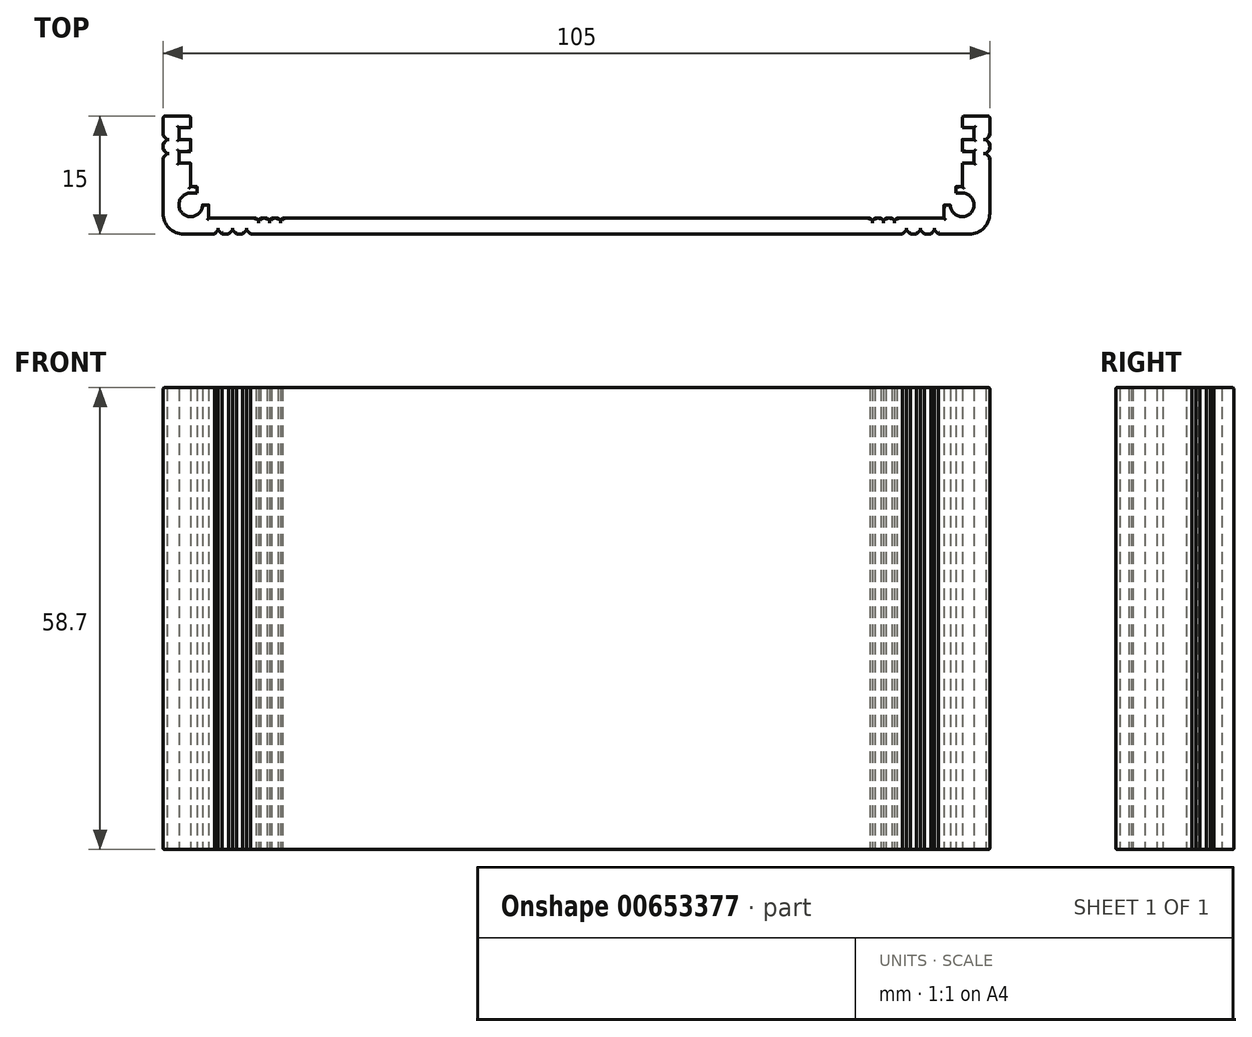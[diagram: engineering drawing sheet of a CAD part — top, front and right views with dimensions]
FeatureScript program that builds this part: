
annotation { "Feature Type Name" : "Feature", "Feature Type Description" : "" }
export const myFeature = defineFeature(function(context is Context, id is Id, definition is map)
    precondition{}
    {
        {
            var Q0;
            Q0=qCreatedBy(makeId("Top.planeOp"),FACE);
            var sketch = newSketch(context, id + "F0", { "sketchPlane" : qUnion([Q0])});
            skLineSegment(sketch, "E0.bottom", {"start": v(52.5, 15) * mm, "end": v(-52.5, 15) * mm, "construction": true});
            skLineSegment(sketch, "E0.top", {"start": v(52.5, -15) * mm, "end": v(-52.5, -15) * mm, "construction": true});
            skLineSegment(sketch, "E0.left", {"start": v(52.5, 15) * mm, "end": v(52.5, -15) * mm, "construction": true});
            skLineSegment(sketch, "E0.right", {"start": v(-52.5, 15) * mm, "end": v(-52.5, -15) * mm, "construction": true});
            skPoint(sketch, "E0.middle", {"position": v(0, 0) * mm});
            skLineSegment(sketch, "E1", {"start": v(-52.5, -15) * mm, "end": v(-46, -15) * mm});
            skLineSegment(sketch, "E2", {"start": v(-46, -15) * mm, "end": v(-45.5, -14.5) * mm});
            skLineSegment(sketch, "E3", {"start": v(-45.5, -14.5) * mm, "end": v(-45, -15) * mm});
            skLineSegment(sketch, "E4", {"start": v(-45, -15) * mm, "end": v(-44.2, -15) * mm});
            skLineSegment(sketch, "E5", {"start": v(-44.2, -15) * mm, "end": v(-43.7, -14.5) * mm});
            skLineSegment(sketch, "E6", {"start": v(-43.7, -14.5) * mm, "end": v(-43.2, -15) * mm});
            skLineSegment(sketch, "E7", {"start": v(-43.2, -15) * mm, "end": v(-42.4, -15) * mm});
            skLineSegment(sketch, "E8", {"start": v(-42.4, -15) * mm, "end": v(-41.9, -14.5) * mm});
            skLineSegment(sketch, "E9", {"start": v(-41.9, -14.5) * mm, "end": v(-41.4, -15) * mm});
            skLineSegment(sketch, "E10", {"start": v(-41.4, -15) * mm, "end": v(0, -15) * mm});
            skLineSegment(sketch, "E11.MirrorCS", {"start": v(52.5, -15) * mm, "end": v(46, -15) * mm});
            skLineSegment(sketch, "E12.MirrorCS", {"start": v(46, -15) * mm, "end": v(45.5, -14.5) * mm});
            skLineSegment(sketch, "E13.MirrorCS", {"start": v(45.5, -14.5) * mm, "end": v(45, -15) * mm});
            skLineSegment(sketch, "E14.MirrorCS", {"start": v(45, -15) * mm, "end": v(44.2, -15) * mm});
            skLineSegment(sketch, "E15.MirrorCS", {"start": v(44.2, -15) * mm, "end": v(43.7, -14.5) * mm});
            skLineSegment(sketch, "E16.MirrorCS", {"start": v(43.7, -14.5) * mm, "end": v(43.2, -15) * mm});
            skLineSegment(sketch, "E17.MirrorCS", {"start": v(43.2, -15) * mm, "end": v(42.4, -15) * mm});
            skLineSegment(sketch, "E18.MirrorCS", {"start": v(42.4, -15) * mm, "end": v(41.9, -14.5) * mm});
            skLineSegment(sketch, "E19.MirrorCS", {"start": v(41.9, -14.5) * mm, "end": v(41.4, -15) * mm});
            skLineSegment(sketch, "E20.MirrorCS", {"start": v(41.4, -15) * mm, "end": v(0, -15) * mm});
            skLineSegment(sketch, "E21", {"start": v(-52.5, 0) * mm, "end": v(-52.5, -2.5) * mm});
            skLineSegment(sketch, "E22", {"start": v(-52.5, -2.5) * mm, "end": v(-52, -3) * mm});
            skLineSegment(sketch, "E23", {"start": v(-52, -3) * mm, "end": v(-52.5, -3.5) * mm});
            skLineSegment(sketch, "E24", {"start": v(-52.5, -3.5) * mm, "end": v(-52.5, -4.3) * mm});
            skLineSegment(sketch, "E25", {"start": v(-52.5, -4.3) * mm, "end": v(-52, -4.8) * mm});
            skLineSegment(sketch, "E26", {"start": v(-52, -4.8) * mm, "end": v(-52.5, -5.3) * mm});
            skLineSegment(sketch, "E27", {"start": v(-52.5, -5.3) * mm, "end": v(-52.5, -15) * mm});
            skLineSegment(sketch, "E28.MirrorCS", {"start": v(52.5, 0) * mm, "end": v(52.5, -2.5) * mm});
            skLineSegment(sketch, "E29.MirrorCS", {"start": v(52.5, -2.5) * mm, "end": v(52, -3) * mm});
            skLineSegment(sketch, "E30.MirrorCS", {"start": v(52, -3) * mm, "end": v(52.5, -3.5) * mm});
            skLineSegment(sketch, "E31.MirrorCS", {"start": v(52.5, -4.3) * mm, "end": v(52, -4.8) * mm});
            skLineSegment(sketch, "E32.MirrorCS", {"start": v(52.5, -3.5) * mm, "end": v(52.5, -4.3) * mm});
            skLineSegment(sketch, "E33.MirrorCS", {"start": v(52, -4.8) * mm, "end": v(52.5, -5.3) * mm});
            skLineSegment(sketch, "E34.MirrorCS", {"start": v(52.5, -5.3) * mm, "end": v(52.5, -15) * mm});
            skLineSegment(sketch, "E35", {"start": v(-52.5, 0) * mm, "end": v(-49, 0) * mm});
            skLineSegment(sketch, "E36", {"start": v(-49, 0) * mm, "end": v(-49, -1.5) * mm});
            skLineSegment(sketch, "E37", {"start": v(-49, -1.5) * mm, "end": v(-50.5, -1.5) * mm});
            skLineSegment(sketch, "E38", {"start": v(-50.5, -1.5) * mm, "end": v(-50.5, -3) * mm});
            skLineSegment(sketch, "E39", {"start": v(-50.5, -3) * mm, "end": v(-49, -3) * mm});
            skLineSegment(sketch, "E40", {"start": v(-49, -3) * mm, "end": v(-49, -4.5) * mm});
            skLineSegment(sketch, "E41", {"start": v(-49, -4.5) * mm, "end": v(-50.5, -4.5) * mm});
            skLineSegment(sketch, "E42", {"start": v(-50.5, -4.5) * mm, "end": v(-50.5, -6) * mm});
            skLineSegment(sketch, "E43", {"start": v(-50.5, -6) * mm, "end": v(-49, -6) * mm});
            skLineSegment(sketch, "E44", {"start": v(-49, -6) * mm, "end": v(-49, -9) * mm});
            skCircle(sketch, "E45", {"center": v(-49, -11.3) * mm, "radius": 1.5 * mm, "construction": true});
            skPoint(sketch, "E45.second.point", {"position": v(-49, -12.8) * mm});
            skPoint(sketch, "E45.third.point", {"position": v(-47.5, -11.3) * mm});
            skLineSegment(sketch, "E46", {"start": v(-49, -12.8) * mm, "end": v(-49, -9.8) * mm, "construction": true});
            skArc(sketch, "E47", {"start": v(-49, -9.8) * mm, "mid": v(-50.06, -12.36) * mm, "end": v(-47.5, -11.3) * mm});
            skLineSegment(sketch, "E48", {"start": v(-47.5, -11.3) * mm, "end": v(-47.5, -11.3) * mm});
            skLineSegment(sketch, "E49", {"start": v(-46.7, -13) * mm, "end": v(-40.7, -13) * mm});
            skLineSegment(sketch, "E50", {"start": v(-40.7, -13) * mm, "end": v(-40.4, -13.3) * mm});
            skLineSegment(sketch, "E51", {"start": v(-40.4, -13.3) * mm, "end": v(-40.1, -13) * mm});
            skLineSegment(sketch, "E52", {"start": v(-40.1, -13) * mm, "end": v(-39.3, -13) * mm});
            skLineSegment(sketch, "E53", {"start": v(-39.3, -13) * mm, "end": v(-39, -13.3) * mm});
            skLineSegment(sketch, "E54", {"start": v(-39, -13.3) * mm, "end": v(-38.7, -13) * mm});
            skLineSegment(sketch, "E55", {"start": v(-38.7, -13) * mm, "end": v(-37.9, -13) * mm});
            skLineSegment(sketch, "E56", {"start": v(-37.9, -13) * mm, "end": v(-37.6, -13.3) * mm});
            skLineSegment(sketch, "E57", {"start": v(-37.6, -13.3) * mm, "end": v(-37.3, -13) * mm});
            skLineSegment(sketch, "E58", {"start": v(-37.3, -13) * mm, "end": v(0, -13) * mm});
            skLineSegment(sketch, "E59", {"start": v(-47.5, -11.3) * mm, "end": v(-46.7, -11.3) * mm});
            skLineSegment(sketch, "E60", {"start": v(-46.7, -11.3) * mm, "end": v(-46.7, -13) * mm});
            skLineSegment(sketch, "E61.MirrorCS", {"start": v(37.3, -13) * mm, "end": v(0, -13) * mm});
            skLineSegment(sketch, "E62.MirrorCS", {"start": v(37.6, -13.3) * mm, "end": v(37.3, -13) * mm});
            skLineSegment(sketch, "E63.MirrorCS", {"start": v(37.9, -13) * mm, "end": v(37.6, -13.3) * mm});
            skLineSegment(sketch, "E64.MirrorCS", {"start": v(39, -13.3) * mm, "end": v(38.7, -13) * mm});
            skLineSegment(sketch, "E65.MirrorCS", {"start": v(39.3, -13) * mm, "end": v(39, -13.3) * mm});
            skLineSegment(sketch, "E66.MirrorCS", {"start": v(40.4, -13.3) * mm, "end": v(40.1, -13) * mm});
            skLineSegment(sketch, "E67.MirrorCS", {"start": v(40.7, -13) * mm, "end": v(40.4, -13.3) * mm});
            skLineSegment(sketch, "E68.MirrorCS", {"start": v(46.7, -13) * mm, "end": v(40.7, -13) * mm});
            skLineSegment(sketch, "E69.MirrorCS", {"start": v(46.7, -11.3) * mm, "end": v(46.7, -13) * mm});
            skLineSegment(sketch, "E70.MirrorCS", {"start": v(49, -6) * mm, "end": v(49, -9) * mm});
            skLineSegment(sketch, "E71.MirrorCS", {"start": v(50.5, -6) * mm, "end": v(49, -6) * mm});
            skLineSegment(sketch, "E72.MirrorCS", {"start": v(50.5, -4.5) * mm, "end": v(50.5, -6) * mm});
            skLineSegment(sketch, "E73.MirrorCS", {"start": v(49, -4.5) * mm, "end": v(50.5, -4.5) * mm});
            skLineSegment(sketch, "E74.MirrorCS", {"start": v(49, -3) * mm, "end": v(49, -4.5) * mm});
            skLineSegment(sketch, "E75.MirrorCS", {"start": v(50.5, -3) * mm, "end": v(49, -3) * mm});
            skLineSegment(sketch, "E76.MirrorCS", {"start": v(50.5, -1.5) * mm, "end": v(50.5, -3) * mm});
            skLineSegment(sketch, "E77.MirrorCS", {"start": v(49, -1.5) * mm, "end": v(50.5, -1.5) * mm});
            skLineSegment(sketch, "E78.MirrorCS", {"start": v(49, 0) * mm, "end": v(49, -1.5) * mm});
            skLineSegment(sketch, "E79.MirrorCS", {"start": v(52.5, 0) * mm, "end": v(49, 0) * mm});
            skLineSegment(sketch, "E80.MirrorCS", {"start": v(38.7, -13) * mm, "end": v(37.9, -13) * mm});
            skLineSegment(sketch, "E81.MirrorCS", {"start": v(40.1, -13) * mm, "end": v(39.3, -13) * mm});
            skLineSegment(sketch, "E82", {"start": v(-49, -9) * mm, "end": v(-48.2, -9) * mm});
            skLineSegment(sketch, "E83", {"start": v(-48.2, -9) * mm, "end": v(-48.2, -9.8) * mm});
            skLineSegment(sketch, "E84", {"start": v(-48.2, -9.8) * mm, "end": v(-49, -9.8) * mm});
            skLineSegment(sketch, "E85", {"start": v(-50.5, -11.3) * mm, "end": v(-47.5, -11.3) * mm, "construction": true});
            skLineSegment(sketch, "E86", {"start": v(-50.5, -11.3) * mm, "end": v(-50.5, -1.5) * mm, "construction": true});
            skArc(sketch, "E87.MirrorCS", {"start": v(49, -9.8) * mm, "mid": v(50.06, -12.36) * mm, "end": v(47.5, -11.3) * mm});
            skLineSegment(sketch, "E88.MirrorCS", {"start": v(49, -9) * mm, "end": v(48.2, -9) * mm});
            skLineSegment(sketch, "E89.MirrorCS", {"start": v(48.2, -9.8) * mm, "end": v(49, -9.8) * mm});
            skLineSegment(sketch, "E90.MirrorCS", {"start": v(48.2, -9) * mm, "end": v(48.2, -9.8) * mm});
            skLineSegment(sketch, "E91.MirrorCS", {"start": v(47.5, -11.3) * mm, "end": v(46.7, -11.3) * mm});
            skSolve(sketch);
        }
        {
            var Q0;
            Q0=makeQuery(id+"F0.imprint","IMPRINT",FACE,{"disambiguationData":[TD([[makeQuery(id+"F0.imprint","IMPRINT",EDGE,{"derivedFrom":sQuery(id+"F0.wireOp",EDGE,"E1")}),1.0]])]});
            extrude(context, id + "F1", {"entities" : qUnion([Q0]), "depth" : 58.7 * mm, "offsetDistance" : 25.4 * mm});
        }
        {
            var Q0;
            Q0=makeQuery(id+"F1.opExtrude","CAP_FACE",FACE,{"disambiguationData":[OSD([sQuery(id+"F0.wireOp",EDGE,"E1"),sQuery(id+"F0.wireOp",EDGE,"E2"),sQuery(id+"F0.wireOp",EDGE,"E3"),sQuery(id+"F0.wireOp",EDGE,"E4"),sQuery(id+"F0.wireOp",EDGE,"E5"),sQuery(id+"F0.wireOp",EDGE,"E6"),sQuery(id+"F0.wireOp",EDGE,"E7"),sQuery(id+"F0.wireOp",EDGE,"E8"),sQuery(id+"F0.wireOp",EDGE,"E9"),sQuery(id+"F0.wireOp",EDGE,"E10"),sQuery(id+"F0.wireOp",EDGE,"E11.MirrorCS"),sQuery(id+"F0.wireOp",EDGE,"E12.MirrorCS"),sQuery(id+"F0.wireOp",EDGE,"E13.MirrorCS"),sQuery(id+"F0.wireOp",EDGE,"E14.MirrorCS"),sQuery(id+"F0.wireOp",EDGE,"E15.MirrorCS"),sQuery(id+"F0.wireOp",EDGE,"E16.MirrorCS"),sQuery(id+"F0.wireOp",EDGE,"E17.MirrorCS"),sQuery(id+"F0.wireOp",EDGE,"E18.MirrorCS"),sQuery(id+"F0.wireOp",EDGE,"E19.MirrorCS"),sQuery(id+"F0.wireOp",EDGE,"E20.MirrorCS"),sQuery(id+"F0.wireOp",EDGE,"E21"),sQuery(id+"F0.wireOp",EDGE,"E22"),sQuery(id+"F0.wireOp",EDGE,"E23"),sQuery(id+"F0.wireOp",EDGE,"E24"),sQuery(id+"F0.wireOp",EDGE,"E25"),sQuery(id+"F0.wireOp",EDGE,"E26"),sQuery(id+"F0.wireOp",EDGE,"E27"),sQuery(id+"F0.wireOp",EDGE,"E28.MirrorCS"),sQuery(id+"F0.wireOp",EDGE,"E29.MirrorCS"),sQuery(id+"F0.wireOp",EDGE,"E30.MirrorCS"),sQuery(id+"F0.wireOp",EDGE,"E31.MirrorCS"),sQuery(id+"F0.wireOp",EDGE,"E32.MirrorCS"),sQuery(id+"F0.wireOp",EDGE,"E33.MirrorCS"),sQuery(id+"F0.wireOp",EDGE,"E34.MirrorCS"),sQuery(id+"F0.wireOp",EDGE,"E35"),sQuery(id+"F0.wireOp",EDGE,"E36"),sQuery(id+"F0.wireOp",EDGE,"E37"),sQuery(id+"F0.wireOp",EDGE,"E38"),sQuery(id+"F0.wireOp",EDGE,"E39"),sQuery(id+"F0.wireOp",EDGE,"E40"),sQuery(id+"F0.wireOp",EDGE,"E41"),sQuery(id+"F0.wireOp",EDGE,"E42"),sQuery(id+"F0.wireOp",EDGE,"E43"),sQuery(id+"F0.wireOp",EDGE,"E44"),sQuery(id+"F0.wireOp",EDGE,"E47"),sQuery(id+"F0.wireOp",EDGE,"E49"),sQuery(id+"F0.wireOp",EDGE,"E50"),sQuery(id+"F0.wireOp",EDGE,"E51"),sQuery(id+"F0.wireOp",EDGE,"E52"),sQuery(id+"F0.wireOp",EDGE,"E53"),sQuery(id+"F0.wireOp",EDGE,"E54"),sQuery(id+"F0.wireOp",EDGE,"E55"),sQuery(id+"F0.wireOp",EDGE,"E56"),sQuery(id+"F0.wireOp",EDGE,"E57"),sQuery(id+"F0.wireOp",EDGE,"E58"),sQuery(id+"F0.wireOp",EDGE,"E59"),sQuery(id+"F0.wireOp",EDGE,"E60"),sQuery(id+"F0.wireOp",EDGE,"E61.MirrorCS"),sQuery(id+"F0.wireOp",EDGE,"E62.MirrorCS"),sQuery(id+"F0.wireOp",EDGE,"E63.MirrorCS"),sQuery(id+"F0.wireOp",EDGE,"E64.MirrorCS"),sQuery(id+"F0.wireOp",EDGE,"E65.MirrorCS"),sQuery(id+"F0.wireOp",EDGE,"E66.MirrorCS"),sQuery(id+"F0.wireOp",EDGE,"E67.MirrorCS"),sQuery(id+"F0.wireOp",EDGE,"E68.MirrorCS"),sQuery(id+"F0.wireOp",EDGE,"E69.MirrorCS"),sQuery(id+"F0.wireOp",EDGE,"E70.MirrorCS"),sQuery(id+"F0.wireOp",EDGE,"E71.MirrorCS"),sQuery(id+"F0.wireOp",EDGE,"E72.MirrorCS"),sQuery(id+"F0.wireOp",EDGE,"E73.MirrorCS"),sQuery(id+"F0.wireOp",EDGE,"E74.MirrorCS"),sQuery(id+"F0.wireOp",EDGE,"E75.MirrorCS"),sQuery(id+"F0.wireOp",EDGE,"E76.MirrorCS"),sQuery(id+"F0.wireOp",EDGE,"E77.MirrorCS"),sQuery(id+"F0.wireOp",EDGE,"E78.MirrorCS"),sQuery(id+"F0.wireOp",EDGE,"E79.MirrorCS"),sQuery(id+"F0.wireOp",EDGE,"E80.MirrorCS"),sQuery(id+"F0.wireOp",EDGE,"E81.MirrorCS"),sQuery(id+"F0.wireOp",EDGE,"E82"),sQuery(id+"F0.wireOp",EDGE,"E83"),sQuery(id+"F0.wireOp",EDGE,"E84"),sQuery(id+"F0.wireOp",EDGE,"E87.MirrorCS"),sQuery(id+"F0.wireOp",EDGE,"E88.MirrorCS"),sQuery(id+"F0.wireOp",EDGE,"E89.MirrorCS"),sQuery(id+"F0.wireOp",EDGE,"E90.MirrorCS"),sQuery(id+"F0.wireOp",EDGE,"E91.MirrorCS")])],"isStart":false});
            fillet(context, id + "F2", {"entities" : qUnion([Q0]), "radius" : 0.2 * mm, "tangentPropagation" : true, "allowEdgeOverflow" : false});
        }
        {
            var Q0;
            Q0=makeQuery(id+"F1.opExtrude","CAP_FACE",FACE,{"disambiguationData":[OSD([sQuery(id+"F0.wireOp",EDGE,"E1"),sQuery(id+"F0.wireOp",EDGE,"E2"),sQuery(id+"F0.wireOp",EDGE,"E3"),sQuery(id+"F0.wireOp",EDGE,"E4"),sQuery(id+"F0.wireOp",EDGE,"E5"),sQuery(id+"F0.wireOp",EDGE,"E6"),sQuery(id+"F0.wireOp",EDGE,"E7"),sQuery(id+"F0.wireOp",EDGE,"E8"),sQuery(id+"F0.wireOp",EDGE,"E9"),sQuery(id+"F0.wireOp",EDGE,"E10"),sQuery(id+"F0.wireOp",EDGE,"E11.MirrorCS"),sQuery(id+"F0.wireOp",EDGE,"E12.MirrorCS"),sQuery(id+"F0.wireOp",EDGE,"E13.MirrorCS"),sQuery(id+"F0.wireOp",EDGE,"E14.MirrorCS"),sQuery(id+"F0.wireOp",EDGE,"E15.MirrorCS"),sQuery(id+"F0.wireOp",EDGE,"E16.MirrorCS"),sQuery(id+"F0.wireOp",EDGE,"E17.MirrorCS"),sQuery(id+"F0.wireOp",EDGE,"E18.MirrorCS"),sQuery(id+"F0.wireOp",EDGE,"E19.MirrorCS"),sQuery(id+"F0.wireOp",EDGE,"E20.MirrorCS"),sQuery(id+"F0.wireOp",EDGE,"E21"),sQuery(id+"F0.wireOp",EDGE,"E22"),sQuery(id+"F0.wireOp",EDGE,"E23"),sQuery(id+"F0.wireOp",EDGE,"E24"),sQuery(id+"F0.wireOp",EDGE,"E25"),sQuery(id+"F0.wireOp",EDGE,"E26"),sQuery(id+"F0.wireOp",EDGE,"E27"),sQuery(id+"F0.wireOp",EDGE,"E28.MirrorCS"),sQuery(id+"F0.wireOp",EDGE,"E29.MirrorCS"),sQuery(id+"F0.wireOp",EDGE,"E30.MirrorCS"),sQuery(id+"F0.wireOp",EDGE,"E31.MirrorCS"),sQuery(id+"F0.wireOp",EDGE,"E32.MirrorCS"),sQuery(id+"F0.wireOp",EDGE,"E33.MirrorCS"),sQuery(id+"F0.wireOp",EDGE,"E34.MirrorCS"),sQuery(id+"F0.wireOp",EDGE,"E35"),sQuery(id+"F0.wireOp",EDGE,"E36"),sQuery(id+"F0.wireOp",EDGE,"E37"),sQuery(id+"F0.wireOp",EDGE,"E38"),sQuery(id+"F0.wireOp",EDGE,"E39"),sQuery(id+"F0.wireOp",EDGE,"E40"),sQuery(id+"F0.wireOp",EDGE,"E41"),sQuery(id+"F0.wireOp",EDGE,"E42"),sQuery(id+"F0.wireOp",EDGE,"E43"),sQuery(id+"F0.wireOp",EDGE,"E44"),sQuery(id+"F0.wireOp",EDGE,"E47"),sQuery(id+"F0.wireOp",EDGE,"E49"),sQuery(id+"F0.wireOp",EDGE,"E50"),sQuery(id+"F0.wireOp",EDGE,"E51"),sQuery(id+"F0.wireOp",EDGE,"E52"),sQuery(id+"F0.wireOp",EDGE,"E53"),sQuery(id+"F0.wireOp",EDGE,"E54"),sQuery(id+"F0.wireOp",EDGE,"E55"),sQuery(id+"F0.wireOp",EDGE,"E56"),sQuery(id+"F0.wireOp",EDGE,"E57"),sQuery(id+"F0.wireOp",EDGE,"E58"),sQuery(id+"F0.wireOp",EDGE,"E59"),sQuery(id+"F0.wireOp",EDGE,"E60"),sQuery(id+"F0.wireOp",EDGE,"E61.MirrorCS"),sQuery(id+"F0.wireOp",EDGE,"E62.MirrorCS"),sQuery(id+"F0.wireOp",EDGE,"E63.MirrorCS"),sQuery(id+"F0.wireOp",EDGE,"E64.MirrorCS"),sQuery(id+"F0.wireOp",EDGE,"E65.MirrorCS"),sQuery(id+"F0.wireOp",EDGE,"E66.MirrorCS"),sQuery(id+"F0.wireOp",EDGE,"E67.MirrorCS"),sQuery(id+"F0.wireOp",EDGE,"E68.MirrorCS"),sQuery(id+"F0.wireOp",EDGE,"E69.MirrorCS"),sQuery(id+"F0.wireOp",EDGE,"E70.MirrorCS"),sQuery(id+"F0.wireOp",EDGE,"E71.MirrorCS"),sQuery(id+"F0.wireOp",EDGE,"E72.MirrorCS"),sQuery(id+"F0.wireOp",EDGE,"E73.MirrorCS"),sQuery(id+"F0.wireOp",EDGE,"E74.MirrorCS"),sQuery(id+"F0.wireOp",EDGE,"E75.MirrorCS"),sQuery(id+"F0.wireOp",EDGE,"E76.MirrorCS"),sQuery(id+"F0.wireOp",EDGE,"E77.MirrorCS"),sQuery(id+"F0.wireOp",EDGE,"E78.MirrorCS"),sQuery(id+"F0.wireOp",EDGE,"E79.MirrorCS"),sQuery(id+"F0.wireOp",EDGE,"E80.MirrorCS"),sQuery(id+"F0.wireOp",EDGE,"E81.MirrorCS"),sQuery(id+"F0.wireOp",EDGE,"E82"),sQuery(id+"F0.wireOp",EDGE,"E83"),sQuery(id+"F0.wireOp",EDGE,"E84"),sQuery(id+"F0.wireOp",EDGE,"E87.MirrorCS"),sQuery(id+"F0.wireOp",EDGE,"E88.MirrorCS"),sQuery(id+"F0.wireOp",EDGE,"E89.MirrorCS"),sQuery(id+"F0.wireOp",EDGE,"E90.MirrorCS"),sQuery(id+"F0.wireOp",EDGE,"E91.MirrorCS")])],"isStart":true});
            fillet(context, id + "F3", {"entities" : qUnion([Q0]), "radius" : 0.2 * mm, "tangentPropagation" : true, "allowEdgeOverflow" : false});
        }
        {
            var Q0;
            Q0=makeQuery(id+"F1.opExtrude","SWEPT_EDGE",EDGE,{"disambiguationData":[OSD([sQuery(id+"F0.wireOp",EDGE,"E21"),sQuery(id+"F0.wireOp",EDGE,"E35")])]});
            var Q1;
            Q1=makeQuery(id+"F1.opExtrude","SWEPT_EDGE",EDGE,{"disambiguationData":[OSD([sQuery(id+"F0.wireOp",EDGE,"E35"),sQuery(id+"F0.wireOp",EDGE,"E36")])]});
            var Q2;
            Q2=makeQuery(id+"F1.opExtrude","SWEPT_EDGE",EDGE,{"disambiguationData":[OSD([sQuery(id+"F0.wireOp",EDGE,"E78.MirrorCS"),sQuery(id+"F0.wireOp",EDGE,"E79.MirrorCS")])]});
            var Q3;
            Q3=makeQuery(id+"F1.opExtrude","SWEPT_EDGE",EDGE,{"disambiguationData":[OSD([sQuery(id+"F0.wireOp",EDGE,"E28.MirrorCS"),sQuery(id+"F0.wireOp",EDGE,"E79.MirrorCS")])]});
            fillet(context, id + "F4", {"entities" : qUnion([Q0, Q1, Q2, Q3]), "radius" : 0.3 * mm, "tangentPropagation" : true, "allowEdgeOverflow" : false});
        }
        {
            var Q0;
            Q0=makeQuery(id+"F1.opExtrude","SWEPT_EDGE",EDGE,{"disambiguationData":[OSD([sQuery(id+"F0.wireOp",EDGE,"E1"),sQuery(id+"F0.wireOp",EDGE,"E27")])]});
            var Q1;
            Q1=makeQuery(id+"F1.opExtrude","SWEPT_EDGE",EDGE,{"disambiguationData":[OSD([sQuery(id+"F0.wireOp",EDGE,"E11.MirrorCS"),sQuery(id+"F0.wireOp",EDGE,"E34.MirrorCS")])]});
            fillet(context, id + "F5", {"entities" : qUnion([Q0, Q1]), "radius" : 2.6 * mm, "tangentPropagation" : true, "allowEdgeOverflow" : false});
        }
    });
